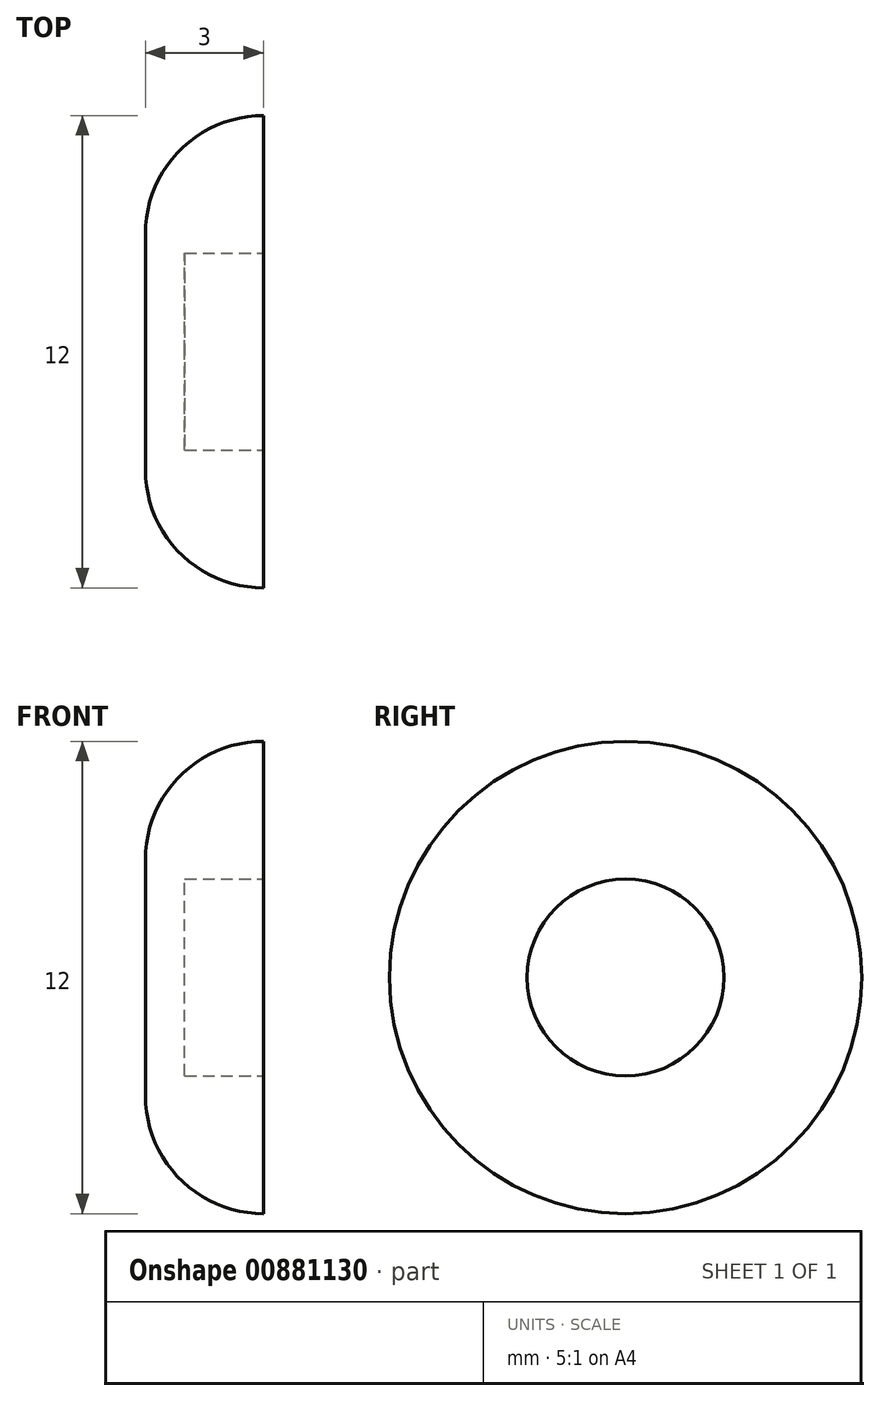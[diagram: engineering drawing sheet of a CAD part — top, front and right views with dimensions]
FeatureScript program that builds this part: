
annotation { "Feature Type Name" : "Feature", "Feature Type Description" : "" }
export const myFeature = defineFeature(function(context is Context, id is Id, definition is map)
    precondition{}
    {
        {
            var Q0;
            Q0=qCreatedBy(makeId("Front.planeOp"),FACE);
            var sketch = newSketch(context, id + "F0", { "sketchPlane" : qUnion([Q0])});
            skLineSegment(sketch, "E0", {"start": v(-2, 0) * mm, "end": v(-3, 0) * mm});
            skLineSegment(sketch, "E1", {"start": v(-3, 0) * mm, "end": v(-3, 3) * mm});
            skLineSegment(sketch, "E2", {"start": v(0, 6) * mm, "end": v(0, 6) * mm});
            skLineSegment(sketch, "E3", {"start": v(0, 6) * mm, "end": v(0, 2.5) * mm});
            skLineSegment(sketch, "E4", {"start": v(0, 2.5) * mm, "end": v(-2, 2.5) * mm});
            skLineSegment(sketch, "E5", {"start": v(-2, 2.5) * mm, "end": v(-2, 0) * mm});
            skPoint(sketch, "E6.visualSharp", {"position": v(-3, 6) * mm});
            skArc(sketch, "E6.filletArc", {"start": v(0, 6) * mm, "mid": v(-2.12, 5.12) * mm, "end": v(-3, 3) * mm});
            skSolve(sketch);
        }
        {
            var Q0;
            Q0=makeQuery(id+"F0.imprint","IMPRINT",FACE,{"disambiguationData":[TD([[makeQuery(id+"F0.imprint","IMPRINT",EDGE,{"derivedFrom":sQuery(id+"F0.wireOp",EDGE,"E0")}),-1.0]])]});
            var Q1;
            Q1=sQuery(id+"F0.wireOp",EDGE,"E0");
            revolve(context, id + "F1", {"surfaceOperationType" : NewSurfaceOperationType.NEW, "entities" : qUnion([Q0]), "axis" : qUnion([Q1]), "revolveType" : RevolveType.FULL});
        }
    });
